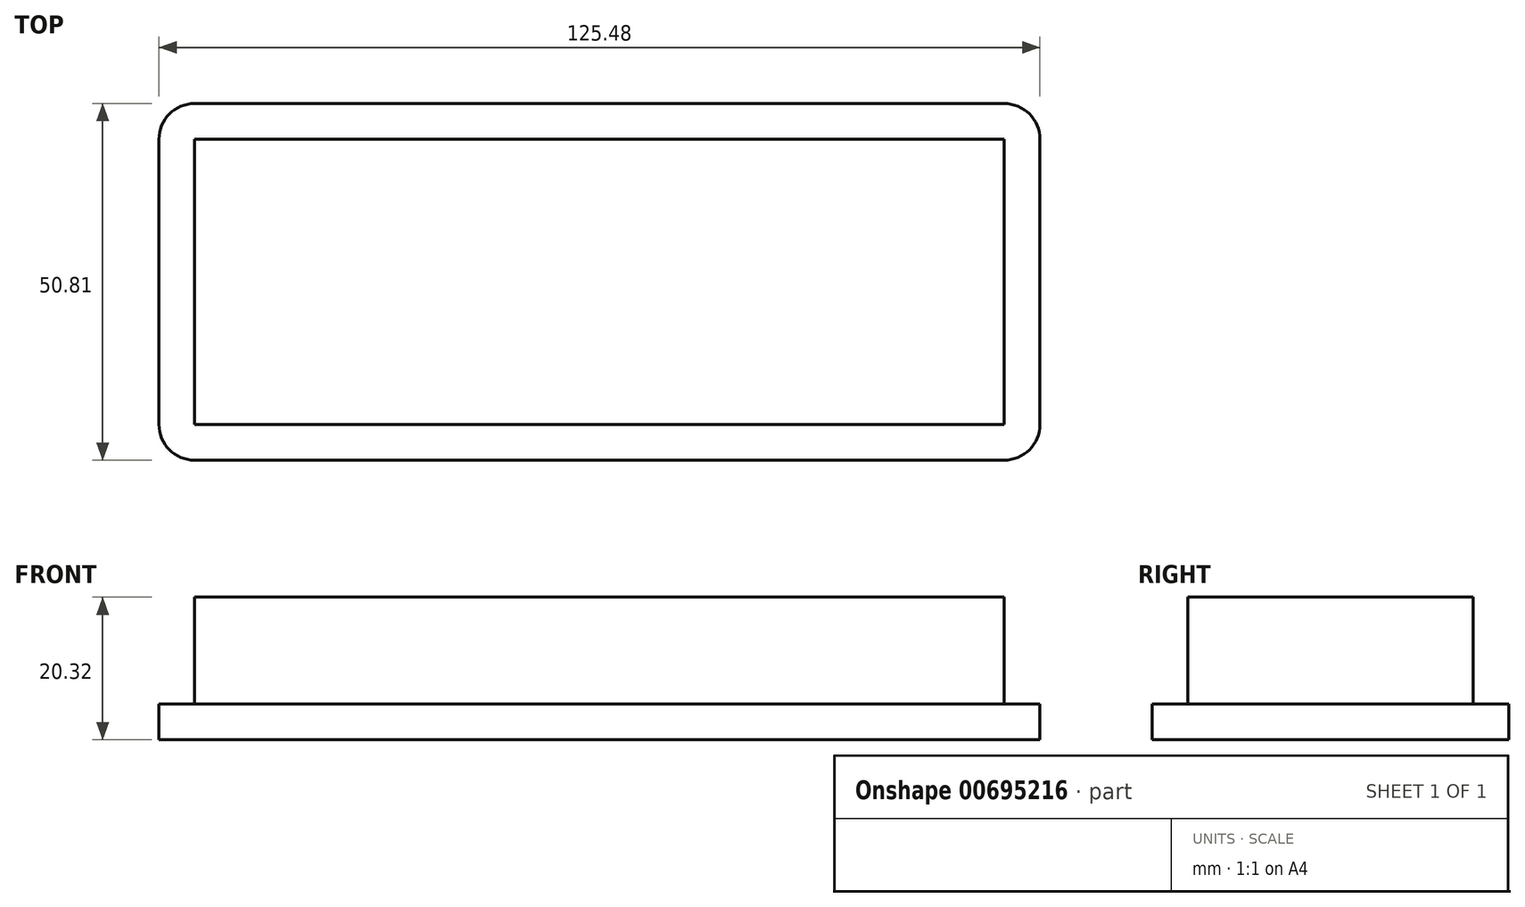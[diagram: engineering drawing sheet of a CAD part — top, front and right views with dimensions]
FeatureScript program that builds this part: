
annotation { "Feature Type Name" : "Feature", "Feature Type Description" : "" }
export const myFeature = defineFeature(function(context is Context, id is Id, definition is map)
    precondition{}
    {
        {
            var Q0;
            Q0=qCreatedBy(makeId("Top.planeOp"),FACE);
            var sketch = newSketch(context, id + "F0", { "sketchPlane" : qUnion([Q0])});
            skLineSegment(sketch, "E0", {"start": v(0, 0) * mm, "end": v(0, 20.95) * mm, "construction": true});
            skLineSegment(sketch, "E1", {"start": v(0, 20.95) * mm, "end": v(-58.04, 20.95) * mm, "construction": true});
            skLineSegment(sketch, "E2.bottom", {"start": v(-58.04, 20.95) * mm, "end": v(57.28, 20.95) * mm});
            skLineSegment(sketch, "E2.top", {"start": v(-58.04, -19.69) * mm, "end": v(57.28, -19.69) * mm});
            skLineSegment(sketch, "E2.left", {"start": v(-58.04, 20.96) * mm, "end": v(-58.04, -19.69) * mm});
            skLineSegment(sketch, "E2.right", {"start": v(57.28, 20.96) * mm, "end": v(57.28, -19.69) * mm});
            skSolve(sketch);
        }
        {
            var Q0;
            Q0=makeQuery(id+"F0.imprint","IMPRINT",FACE,{"disambiguationData":[TD([[makeQuery(id+"F0.imprint","IMPRINT",EDGE,{"derivedFrom":sQuery(id+"F0.wireOp",EDGE,"E2.bottom")}),-1.0]])]});
            extrude(context, id + "F1", {"entities" : qUnion([Q0]), "endBound" : BoundingType.SYMMETRIC, "depth" : 20.32 * mm, "offsetDistance" : 25.4 * mm});
        }
        {
            var Q0;
            Q0=makeQuery(id+"F1.opExtrude","CAP_FACE",FACE,{"disambiguationData":[OSD([sQuery(id+"F0.wireOp",EDGE,"E2.bottom"),sQuery(id+"F0.wireOp",EDGE,"E2.top"),sQuery(id+"F0.wireOp",EDGE,"E2.left"),sQuery(id+"F0.wireOp",EDGE,"E2.right")])],"isStart":true});
            var sketch = newSketch(context, id + "F2", { "sketchPlane" : qUnion([Q0])});
            skLineSegment(sketch, "E3.bottom", {"start": v(-63.12, 24.77) * mm, "end": v(62.36, 24.77) * mm});
            skLineSegment(sketch, "E3.top", {"start": v(-63.12, -26.04) * mm, "end": v(62.36, -26.04) * mm});
            skLineSegment(sketch, "E3.left", {"start": v(-63.12, 24.77) * mm, "end": v(-63.12, -26.04) * mm});
            skLineSegment(sketch, "E3.right", {"start": v(62.36, 24.77) * mm, "end": v(62.36, -26.04) * mm});
            skSolve(sketch);
        }
        {
            var Q0;
            Q0=makeQuery(id+"F2.imprint","IMPRINT",FACE,{"disambiguationData":[TD([[makeQuery(id+"F2.imprint","IMPRINT",EDGE,{"derivedFrom":sQuery(id+"F2.wireOp",EDGE,"E3.bottom")}),-1.0]])]});
            extrude(context, id + "F3", {"entities" : qUnion([Q0]), "operationType" : NewBodyOperationType.ADD, "oppositeDirection" : true, "depth" : 5.08 * mm, "offsetDistance" : 25.4 * mm});
        }
        {
            var Q0;
            Q0=makeQuery(id+"F3.opExtrude","SWEPT_EDGE",EDGE,{"disambiguationData":[OSD([sQuery(id+"F2.wireOp",EDGE,"E3.bottom"),sQuery(id+"F2.wireOp",EDGE,"E3.left")])]});
            var Q1;
            Q1=makeQuery(id+"F3.opExtrude","SWEPT_EDGE",EDGE,{"disambiguationData":[OSD([sQuery(id+"F2.wireOp",EDGE,"E3.bottom"),sQuery(id+"F2.wireOp",EDGE,"E3.right")])]});
            var Q2;
            Q2=makeQuery(id+"F3.opExtrude","SWEPT_EDGE",EDGE,{"disambiguationData":[OSD([sQuery(id+"F2.wireOp",EDGE,"E3.top"),sQuery(id+"F2.wireOp",EDGE,"E3.left")])]});
            var Q3;
            Q3=makeQuery(id+"F3.opExtrude","SWEPT_EDGE",EDGE,{"disambiguationData":[OSD([sQuery(id+"F2.wireOp",EDGE,"E3.top"),sQuery(id+"F2.wireOp",EDGE,"E3.right")])]});
            fillet(context, id + "F4", {"entities" : qUnion([Q0, Q1, Q2, Q3]), "radius" : 5.08 * mm, "tangentPropagation" : true, "allowEdgeOverflow" : false});
        }
    });
